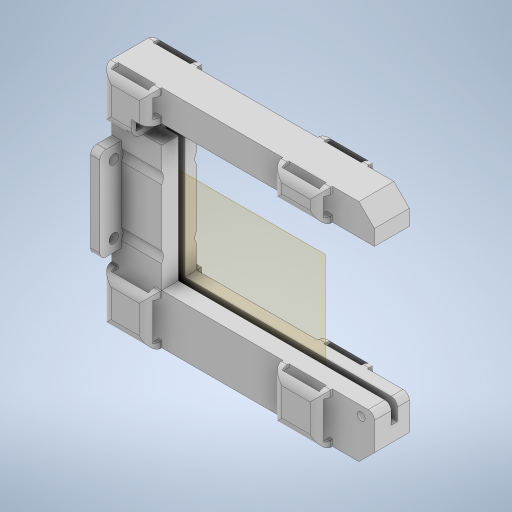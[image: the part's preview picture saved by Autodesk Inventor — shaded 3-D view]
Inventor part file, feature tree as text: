
AUTODESK INVENTOR PART (.ipt)
format: ipt  version: 2024 (Build 280153000, 153)  size: 1,360,384 bytes
history: native  units: mm
features: projected_geometry x31, sketch x19, extrude x18, plane x4, mirror x3, pattern_linear x3, chamfer x2, fillet x2
ambient origin geometry x8: Origin, YZ Plane, XZ Plane, XY Plane, X Axis, Y Axis, Z Axis, Center Point
bodies: Solid1 (feature_tree)
feature tree (82):
  extrude  "Extrusion1"  Depth=10.0mm
  extrude  "Extrusion2"  Depth=6.0mm
  extrude  "Extrusion5"  Depth=6.0mm
  extrude  "Extrusion6"  Depth=3.875mm
  extrude  "Extrusion7"  Depth=10.0mm
  extrude  "Extrusion9"  Depth=2.0mm
  extrude  "Extrusion10"  Depth=5.375mm
  plane  "Work Plane4"
  mirror  "Mirror5"
  extrude  "Extrusion24"  Depth=4.0mm
  extrude  "Extrusion18"  Depth=11.25mm
  pattern_linear  "Rectangular Pattern2"  Spacing1=74.5mm  [1 undecoded]
  pattern_linear  "Rectangular Pattern3"  Spacing1=0.0mm  [1 undecoded]
  plane  "Work Plane3"
  mirror  "Mirror2"
  extrude  "Extrusion19"  Depth=2.25mm
  extrude  "Extrusion27"  Depth=11.25mm TaperAngle=0.0deg
  plane  "Work Plane1"
  plane  "Work Plane2"
  chamfer  "Chamfer2"  Distance=16.0mm
  pattern_linear  "Rectangular Pattern6"  Spacing1=16.0mm  [1 undecoded]
  mirror  "Mirror7"
  chamfer  "Chamfer3"  [1 undecoded]
  fillet  "Fillet3"  Radius=5.0mm
  extrude  "Extrusion28"  Depth=2.25mm
  fillet  "Fillet4"  Radius=5.0mm
  extrude  "Extrusion29"  TaperAngle=0.0deg  [1 undecoded]
  extrude  "Extrusion30"  Depth=1.5mm
  extrude  "Extrusion31"  TaperAngle=0.0deg  [1 undecoded]
  sketch  "Sketch32"  dims[d67=10.0mm]
  extrude  "Extrusion32"  Depth=7.0mm
  extrude  "Extrusion33"  Depth=1.5mm
  extrude  "Extrusion34"  Depth=1.5mm
  sketch  "Sketch1"  dims[d0=52.5mm d1=10.0mm]
  sketch  "Sketch2"  dims[d2=10.0mm d3=6.0mm]
  projected_geometry  "Projected Loop1"
  sketch  "Sketch5"  dims[d6=10.0mm d7=6.0mm]
  projected_geometry  "Projected Loop6"
  projected_geometry  "Projected Loop7"
  sketch  "Sketch6"  dims[d11=10.0mm d22=3.875mm]
  projected_geometry  "Projected Loop8"
  projected_geometry  "Projected Loop9"
  sketch  "Sketch7"  dims[d23=0.0mm d24=10.0mm]
  projected_geometry  "Projected Loop10"
  projected_geometry  "Projected Loop11"
  sketch  "Sketch9"  dims[d25=10.0mm d26=2.0mm]
  projected_geometry  "Projected Loop13"
  sketch  "Sketch10"  dims[d27=0.0mm d49=5.375mm]
  projected_geometry  "Projected Loop14"
  sketch  "Sketch18"  dims[d50=0.0mm d51=4.0mm]
  sketch  "Sketch19"  dims[d52=4.0mm d53=11.25mm d54=5.625mm]
  projected_geometry  "Projected Loop34"
  sketch  "Sketch24"  dims[d58=10.0mm]
  projected_geometry  "Projected Loop39"
  projected_geometry  "Projected Loop40"
  projected_geometry  "Projected Loop45"
  sketch  "Sketch27"  dims[d59=0.0mm]
  projected_geometry  "Projected Loop46"
  projected_geometry  "Projected Loop47"
  sketch  "Sketch28"  dims[d60=4.0mm]
  projected_geometry  "Projected Loop48"
  sketch  "Sketch29"  dims[d61=4.0mm]
  projected_geometry  "Projected Loop49"
  projected_geometry  "Projected Loop50"
  sketch  "Sketch30"  dims[d62=11.25mm d63=5.625mm]
  projected_geometry  "Projected Loop51"
  sketch  "Sketch31"  dims[d64=5.625mm]
  projected_geometry  "Projected Loop52"
  projected_geometry  "Projected Loop53"
  projected_geometry  "Projected Loop54"
  sketch  "Sketch33"  dims[d68=0.0mm]
  projected_geometry  "Projected Loop55"
  projected_geometry  "Projected Loop56"
  projected_geometry  "Projected Loop57"
  projected_geometry  "Projected Loop58"
  sketch  "Sketch34"  dims[d77=28.0mm]
  projected_geometry  "Projected Loop59"
  projected_geometry  "Projected Loop60"
  sketch  "Sketch35"  dims[d78=34.25mm d82=74.5mm d83=0.0mm d84=0.0mm d90=2.25mm d93=11.25mm d94=0.0mm d146=16.0mm d147=16.0mm d148=0.0mm d150=5.0mm d151=0.0mm d152=2.25mm d153=5.0mm d154=0.0mm d155=1.5mm d156=0.0mm d157=7.0mm d158=1.5mm d159=1.5mm d160=0.0mm d161=16.0mm d162=0.0mm d174=16.0mm d176=0.0mm d177=16.0mm d181=20.0mm d183=56.5mm d184=20.0mm d186=55.0mm d210=6.0mm d211=10.0mm d212=10.0mm d213=72.5mm d215=3.5mm d216=5.5mm d218=0.0mm d219=0.0mm d220=7.0mm d221=0.0mm d222=1.5mm d223=2.25mm d224=0.0mm d225=9.0mm d227=2.0mm d228=0.0mm d230=2.25mm d231=1.5mm d232=0.0mm d233=6.155119mm d234=0.0mm d235=2.0mm d236=3.5mm d237=3.5mm d268=74.5mm d270=69.0mm d271=100.0mm d272=0.0mm d273=0.0mm d274=2.5mm d275=2.5mm d276=2.25mm d277=2.0mm d278=2.0mm d279=9.0mm d280=0.0mm d281=3.5mm d282=3.5mm d283=1.5mm d284=16.0mm d285=0.0mm d286=1.0mm d287=2.0mm d288=45.0deg d289=20.0mm d291=55.0mm d292=20.0mm d294=56.5mm d295=5.0mm d296=2.0mm d297=45.0deg d298=2.0mm d299=0.0mm d300=30.0mm d302=25.0mm d305=0.0mm d306=16.104mm d307=22.0mm d308=3.05mm d309=3.05mm d310=3.05mm d311=3.05mm d312=3.0mm d313=0.0mm d314=2.0mm d315=6.0mm d316=6.0mm d317=6.0mm d318=6.0mm d319=0.0mm d320=0.0mm d321=20.5mm d322=7.0mm d323=24.0mm d324=0.0mm d325=24.0mm d326=4.0mm d327=0.0mm d328=0.0mm d329=0.0mm d330=0.0mm d331=0.0mm d332=0.0mm d333=2.0mm d334=2.0mm d335=0.0mm d336=2.0mm d337=0.0mm d338=0.0mm d339=2.0mm d340=2.0mm d341=0.0mm d342=0.0mm d343=0.0mm d344=2.0mm d345=2.0mm d346=5.0mm d347=0.0mm d348=20.0mm d349=0.0mm d350=20.0mm d351=0.0mm d352=2.0mm d353=9.035763mm d354=2.25mm d355=1.5mm d356=3.5mm d357=3.5mm d358=3.5mm d359=3.5mm d360=3.5mm d361=20.0mm d362=0.0mm d202=0.5mm d203=0.872665mm d204=0.5mm d205=0.872665mm d206=0.872665mm d207=0.5mm d208=0.872665mm]
  projected_geometry  "Projected Loop61"
  projected_geometry  "Projected Loop62"
  projected_geometry  "Projected Loop63"
note: 6 required parameter values undecoded (feature->parameter linkage not recoverable at this tier; creation-order binding heuristic only, values carry confidence <= 0.55)
